# Revit family: PRD_AR_HygieneBagDispenser_HBD91
name_source: partatom
category: Specialty Equipment
units: mm (PartAtom-declared; Revit-internal decimal feet)

## family parameters
Cut with Voids When Loaded = No
Host = Face
OmniClass Number = 23.40.20.21
OmniClass Title = Toilet and Bath Specialties
Part Type = Normal
Room Calculation Point = No
Round Connector Dimension = Use Diameter
Shared = No

## types (1)
- HBD91
    AssetType = Fixed
    BIMObjectName = PRD_AR_HygieneBagDispenser_HBD91
    Category = Pr_40_70_22, Dispensers and acceptance units
    Color = Stainless steel
    Default Elevation = 650 mm  [stored 2.13255 ft]
    Description = Sanitary bag dispenser for wall mounting, made of stainless steel, surface satin finished, material thickness 1.2 mm, corners not welded, internal mounting bracket, mounting with pre-attached double-sided adhesive tape or enclosed screws and hanger bolts, including acetone wipe for cleaning the surface to be glued, for boxes with a maximum depth of 17 mm.
    DispenserMaterial = PRD_AR_StainlessSteel_SatinFinished
    DurationUnit = year
    Features = stainless steel, 1.20 mm, satin finished, wall mounting, 95 x 150 x 24 mm (W x H x D)
    FillingQuantity = 30 Pieces
    Finish = Satin finished
    GrossWeight = 0.30 kg
    IfcExportAs = IfcFurnitureType
    IfcExportType = NOTDEFINED
    MainColor = Stainless steel
    Manufacturer = KWC Group Management AG
    ManufacturerName = KWC Group Management AG
    ManufacturerURL = www.kwc-professional.com
    Material = Stainless steel
    Model = HBD91
    ModelNumber = 3600008946
    ModelReference = HBD91
    Name = Hygiene bag dispenser HBD91
    NetWeight = 0.24 kg
    NominalDepth = 22 mm  [stored 0.0721785 ft]
    NominalHeight = 150 mm
    NominalLength = 92 mm  [stored 0.301837 ft]
    NominalWidth = 92 mm  [stored 0.301837 ft]
    ProductInformation = http://pim.kwc.com
    Size = 95x150x24 mm
    Style = Hygiene bag dispenser
    URL = www.kwc-professional.com
    Version = 1
    WarrantyDurationUnit = year

note: [stored X ft] marks values corroborated as IEEE doubles in the binary element streams (Revit-internal decimal feet)

## geometry (parser evidence)
native form markers: Sweep x2
no freeform markers — native parametric forms only
